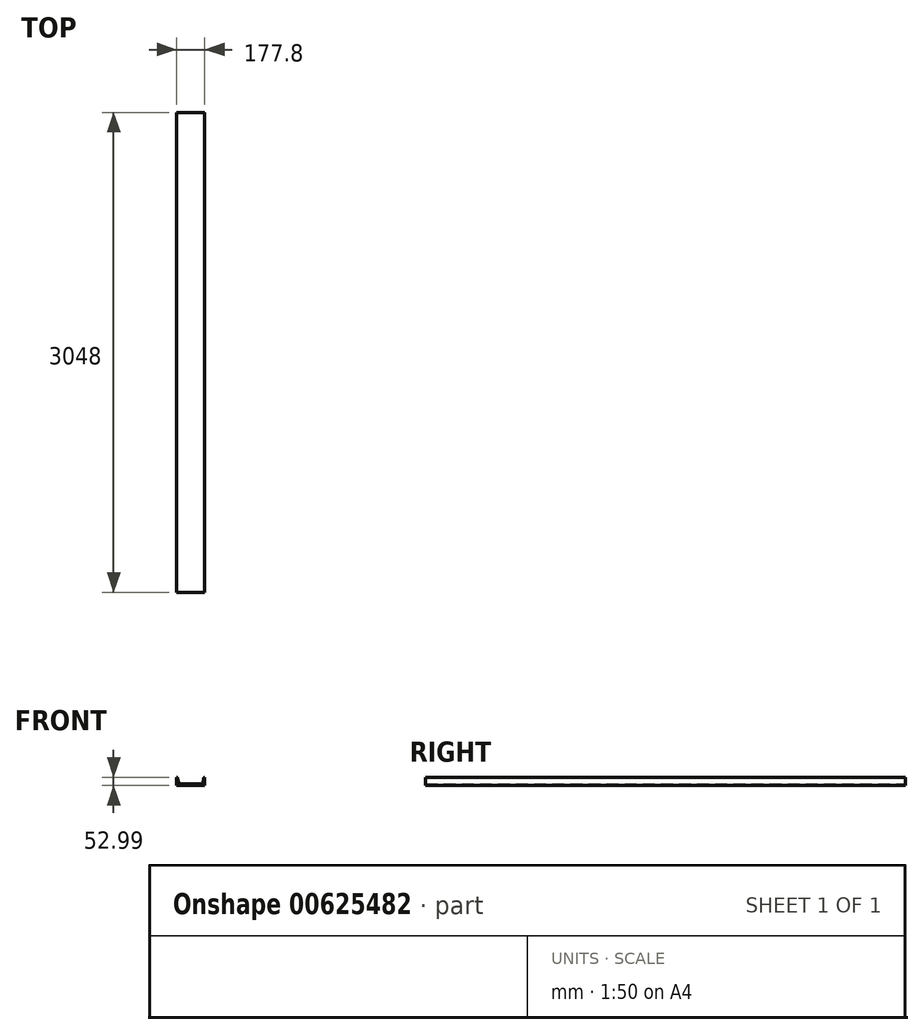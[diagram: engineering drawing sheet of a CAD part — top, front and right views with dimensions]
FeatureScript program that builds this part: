
annotation { "Feature Type Name" : "Feature", "Feature Type Description" : "" }
export const myFeature = defineFeature(function(context is Context, id is Id, definition is map)
    precondition{}
    {
        {
            var Q0;
            Q0=qCreatedBy(makeId("Front.planeOp"),FACE);
            var sketch = newSketch(context, id + "F0", { "sketchPlane" : qUnion([Q0])});
            skLineSegment(sketch, "E0", {"start": v(0, 0) * mm, "end": v(177.8, 0) * mm});
            skLineSegment(sketch, "E1", {"start": v(177.8, 0) * mm, "end": v(177.8, 53.09) * mm});
            skLineSegment(sketch, "E2", {"start": v(179.02, 53.09) * mm, "end": v(177.8, 53.09) * mm});
            skLineSegment(sketch, "E3", {"start": v(171.27, 46.64) * mm, "end": v(165.78, 16.97) * mm});
            skLineSegment(sketch, "E4", {"start": v(158.04, 10.52) * mm, "end": v(19.76, 10.52) * mm});
            skLineSegment(sketch, "E5", {"start": v(0, 53.09) * mm, "end": v(0, 0) * mm});
            skPoint(sketch, "E6.visualSharp", {"position": v(164.6, 10.52) * mm});
            skArc(sketch, "E6.filletArc", {"start": v(158.04, 10.52) * mm, "mid": v(163.08, 12.34) * mm, "end": v(165.78, 16.97) * mm});
            skPoint(sketch, "E7.visualSharp", {"position": v(172.47, 53.09) * mm});
            skArc(sketch, "E7.filletArc", {"start": v(179.02, 53.09) * mm, "mid": v(173.98, 51.27) * mm, "end": v(171.27, 46.64) * mm});
            skPoint(sketch, "E8.visualSharp", {"position": v(13.2, 10.52) * mm});
            skArc(sketch, "E8.filletArc", {"start": v(11.93, 17.55) * mm, "mid": v(14.5, 12.54) * mm, "end": v(19.76, 10.52) * mm});
            skLineSegment(sketch, "E9.MirrorCS", {"start": v(19.76, 10.52) * mm, "end": v(158.04, 10.52) * mm});
            skLineSegment(sketch, "E10.MirrorCS", {"start": v(177.8, 0) * mm, "end": v(0, 0) * mm});
            skArc(sketch, "E11.MirrorCS", {"start": v(-1.22, 53.09) * mm, "mid": v(3.82, 51.27) * mm, "end": v(6.53, 46.64) * mm});
            skLineSegment(sketch, "E12.MirrorCS", {"start": v(6.53, 46.64) * mm, "end": v(12.02, 16.97) * mm});
            skArc(sketch, "E13.MirrorCS", {"start": v(19.76, 10.52) * mm, "mid": v(14.72, 12.34) * mm, "end": v(12.02, 16.97) * mm});
            skPoint(sketch, "E14.start.orphan", {"position": v(8.6, 53.09) * mm});
            skSolve(sketch);
        }
        {
            var Q0;
            {var subQ4=sQuery(id+"F0.wireOp",EDGE,"E3");Q0=makeQuery(id+"F0.imprint","IMPRINT",FACE,{"disambiguationData":[TD([[makeQuery(id+"F0.imprint","IMPRINT",EDGE,{"derivedFrom":subQ4}),1.0]])]});}
            extrude(context, id + "F1", {"entities" : qUnion([Q0]), "depth" : 3048 * mm, "offsetDistance" : 25.4 * mm});
        }
    });
